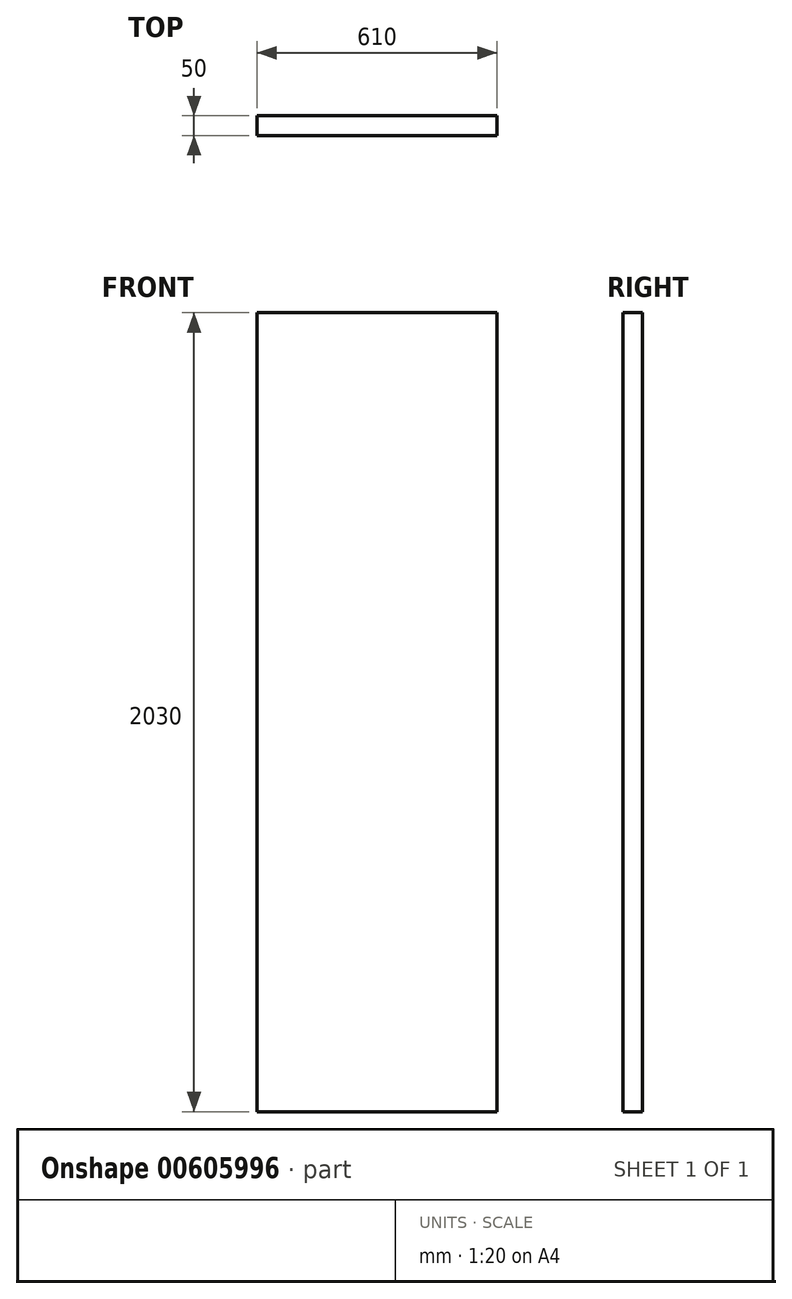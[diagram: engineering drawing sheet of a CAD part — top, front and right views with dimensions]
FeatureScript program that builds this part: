
annotation { "Feature Type Name" : "Feature", "Feature Type Description" : "" }
export const myFeature = defineFeature(function(context is Context, id is Id, definition is map)
    precondition{}
    {
        {
            var Q0;
            Q0=qCreatedBy(makeId("Front.planeOp"),FACE);
            var sketch = newSketch(context, id + "F0", { "sketchPlane" : qUnion([Q0])});
            skLineSegment(sketch, "E0.bottom", {"start": v(555.69, 1985.9) * mm, "end": v(-54.31, 1985.9) * mm});
            skLineSegment(sketch, "E0.top", {"start": v(555.69, -44.1) * mm, "end": v(-54.31, -44.1) * mm});
            skLineSegment(sketch, "E0.left", {"start": v(555.69, 1985.9) * mm, "end": v(555.69, -44.1) * mm});
            skLineSegment(sketch, "E0.right", {"start": v(-54.31, 1985.9) * mm, "end": v(-54.31, -44.1) * mm});
            skSolve(sketch);
        }
        {
            var Q0;
            Q0 = qSketchRegion(id + "F0", true);
            extrude(context, id + "F1", {"entities" : qUnion([Q0]), "depth" : 50 * mm, "offsetDistance" : 25 * mm});
        }
    });
